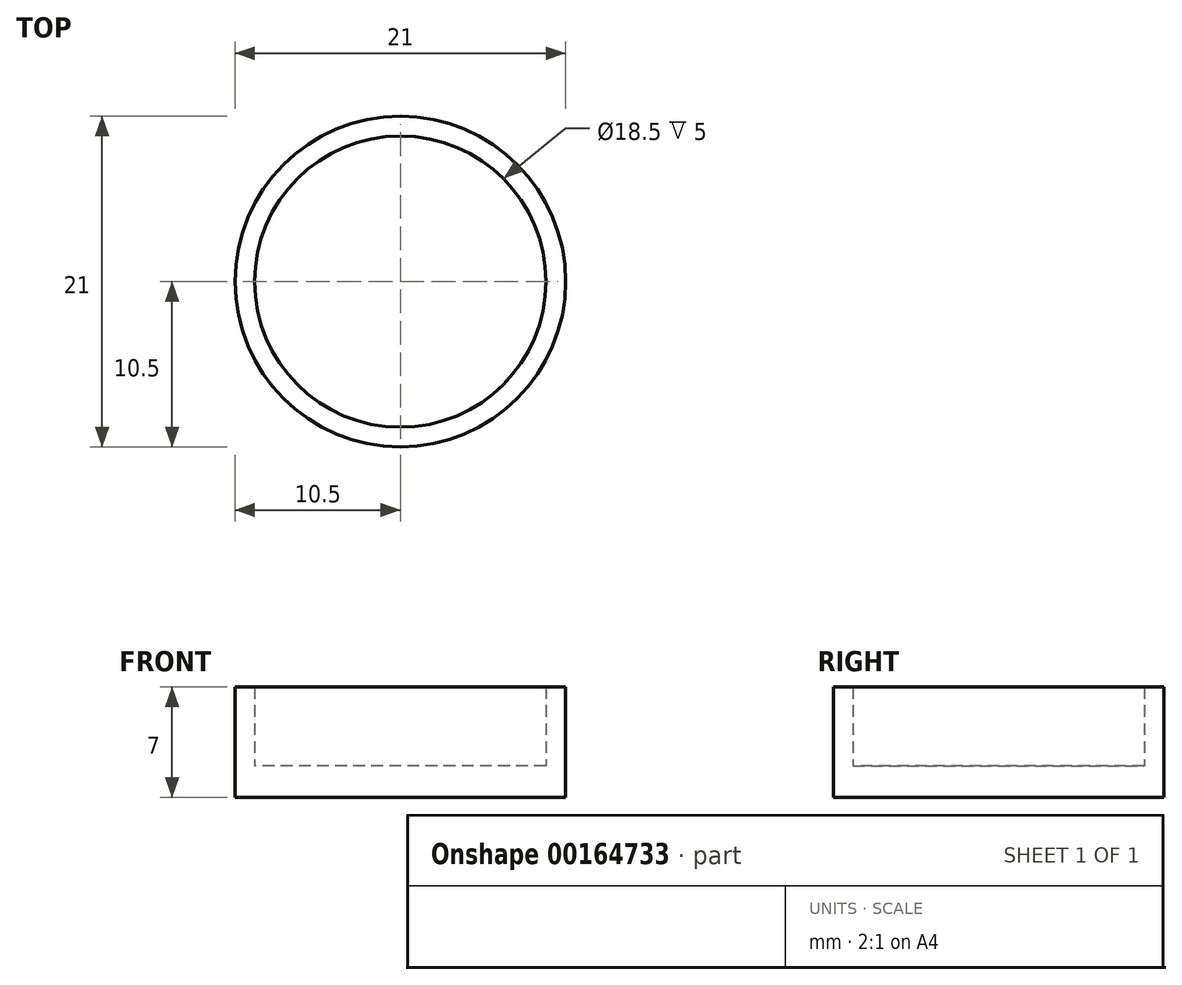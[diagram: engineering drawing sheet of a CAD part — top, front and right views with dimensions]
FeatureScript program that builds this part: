
annotation { "Feature Type Name" : "Feature", "Feature Type Description" : "" }
export const myFeature = defineFeature(function(context is Context, id is Id, definition is map)
    precondition{}
    {
        {
            var Q0;
            Q0=qCreatedBy(makeId("Top.planeOp"),FACE);
            var sketch = newSketch(context, id + "F0", { "sketchPlane" : qUnion([Q0])});
            skCircle(sketch, "E0", {"center": v(0, 0) * mm, "radius": 9.25 * mm});
            skCircle(sketch, "E1", {"center": v(0, 0) * mm, "radius": 10.5 * mm});
            skSolve(sketch);
        }
        {
            var Q0;
            Q0=qSketchRegion(id+"F0",true);
            extrude(context, id + "F1", {"entities" : qUnion([Q0]), "depth" : 7 * mm});
        }
        {
            var Q0;
            Q0=makeQuery(id+"F0.imprint","IMPRINT",FACE,{"disambiguationData":[TD([[makeQuery(id+"F0.imprint","IMPRINT",EDGE,{"derivedFrom":sQuery(id+"F0.wireOp",EDGE,"E0")}),1.0]])]});
            extrude(context, id + "F2", {"entities" : qUnion([Q0]), "operationType" : NewBodyOperationType.ADD, "depth" : 2 * mm});
        }
    });
